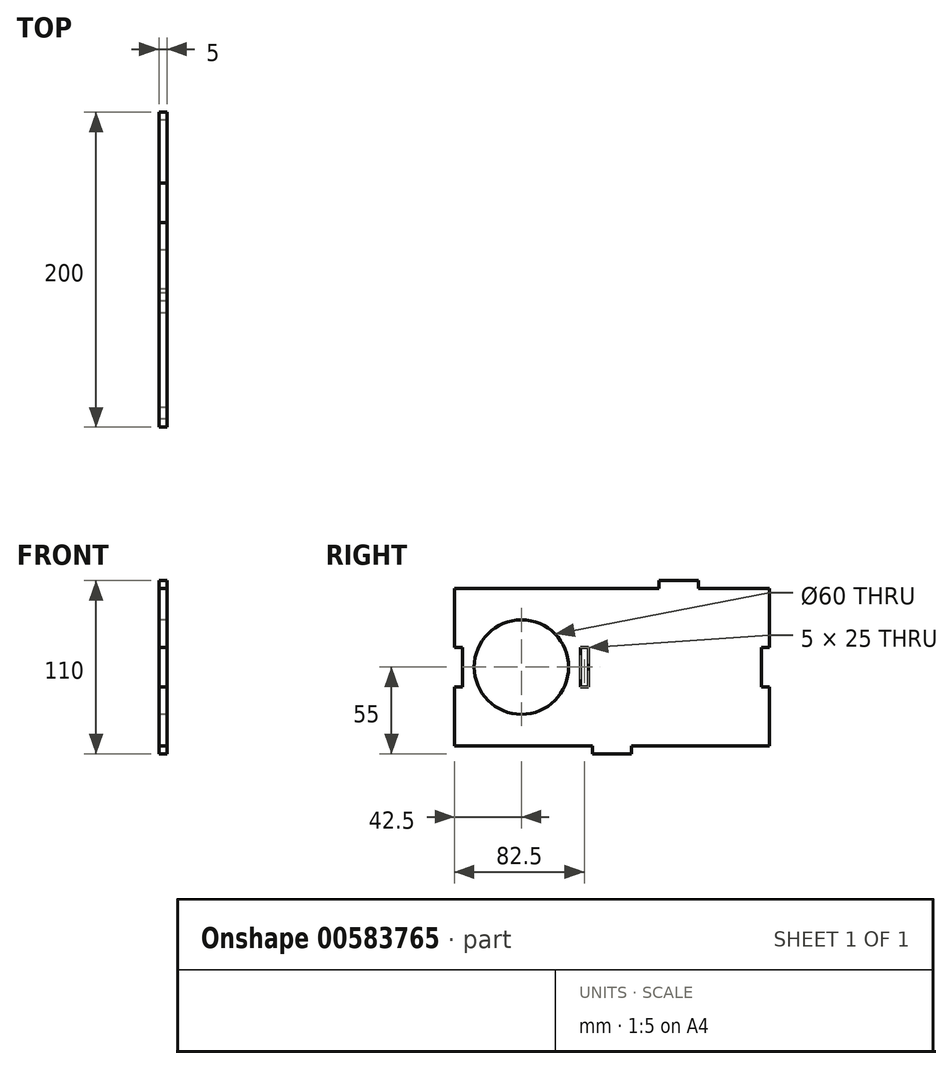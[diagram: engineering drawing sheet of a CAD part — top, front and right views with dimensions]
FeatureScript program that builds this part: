
annotation { "Feature Type Name" : "Feature", "Feature Type Description" : "" }
export const myFeature = defineFeature(function(context is Context, id is Id, definition is map)
    precondition{}
    {
        {
            var Q0;
            Q0=qCreatedBy(makeId("Right.planeOp"),FACE);
            var sketch = newSketch(context, id + "F0", { "sketchPlane" : qUnion([Q0])});
            skLineSegment(sketch, "E0", {"start": v(80.32, 62.5) * mm, "end": v(80.32, 67.5) * mm});
            skLineSegment(sketch, "E1", {"start": v(80.32, 67.5) * mm, "end": v(55.32, 67.5) * mm});
            skLineSegment(sketch, "E2", {"start": v(55.32, 67.5) * mm, "end": v(55.32, 62.5) * mm});
            skLineSegment(sketch, "E3", {"start": v(-74.68, -37.5) * mm, "end": v(12.82, -37.5) * mm});
            skLineSegment(sketch, "E4", {"start": v(12.82, -37.5) * mm, "end": v(12.82, -42.5) * mm});
            skLineSegment(sketch, "E5", {"start": v(12.82, -42.5) * mm, "end": v(37.82, -42.5) * mm});
            skLineSegment(sketch, "E6", {"start": v(37.82, -42.5) * mm, "end": v(37.82, -37.5) * mm});
            skLineSegment(sketch, "E7", {"start": v(37.82, -37.5) * mm, "end": v(125.32, -37.5) * mm});
            skLineSegment(sketch, "E8", {"start": v(-74.68, -37.5) * mm, "end": v(-74.68, 0) * mm});
            skLineSegment(sketch, "E9", {"start": v(-74.68, 0) * mm, "end": v(-69.68, 0) * mm});
            skLineSegment(sketch, "E10", {"start": v(-69.68, 0) * mm, "end": v(-69.68, 25) * mm});
            skLineSegment(sketch, "E11", {"start": v(-69.68, 25) * mm, "end": v(-74.68, 25) * mm});
            skLineSegment(sketch, "E12", {"start": v(125.32, -37.5) * mm, "end": v(125.32, 0) * mm});
            skLineSegment(sketch, "E13", {"start": v(125.32, 0) * mm, "end": v(120.32, 0) * mm});
            skLineSegment(sketch, "E14", {"start": v(120.32, 0) * mm, "end": v(120.32, 25) * mm});
            skLineSegment(sketch, "E15", {"start": v(120.32, 25) * mm, "end": v(125.32, 25) * mm});
            skLineSegment(sketch, "E16", {"start": v(-74.68, 25) * mm, "end": v(-74.68, 62.5) * mm});
            skLineSegment(sketch, "E17", {"start": v(125.32, 25) * mm, "end": v(125.32, 62.5) * mm});
            skLineSegment(sketch, "E18", {"start": v(80.32, 62.5) * mm, "end": v(125.32, 62.5) * mm});
            skLineSegment(sketch, "E19", {"start": v(5.32, 0) * mm, "end": v(5.32, 25) * mm});
            skLineSegment(sketch, "E20", {"start": v(5.32, 25) * mm, "end": v(10.32, 25) * mm});
            skLineSegment(sketch, "E21", {"start": v(10.32, 25) * mm, "end": v(10.32, 0) * mm});
            skLineSegment(sketch, "E22", {"start": v(10.32, 0) * mm, "end": v(5.32, 0) * mm});
            skPoint(sketch, "E23.endSnap0", {"position": v(5.32, 12.5) * mm});
            skCircle(sketch, "E24", {"center": v(-32.18, 12.5) * mm, "radius": 30 * mm});
            skLineSegment(sketch, "E25", {"start": v(-74.68, 62.5) * mm, "end": v(10.32, 62.5) * mm});
            skLineSegment(sketch, "E26", {"start": v(10.32, 62.5) * mm, "end": v(55.32, 62.5) * mm});
            skSolve(sketch);
        }
        {
            var Q0;
            Q0=makeQuery(id+"F0.imprint","IMPRINT",FACE,{"disambiguationData":[TD([[makeQuery(id+"F0.imprint","IMPRINT",EDGE,{"derivedFrom":sQuery(id+"F0.wireOp",EDGE,"E0")}),1.0]])]});
            extrude(context, id + "F1", {"entities" : qUnion([Q0]), "depth" : 5 * mm, "offsetDistance" : 25 * mm});
        }
    });
